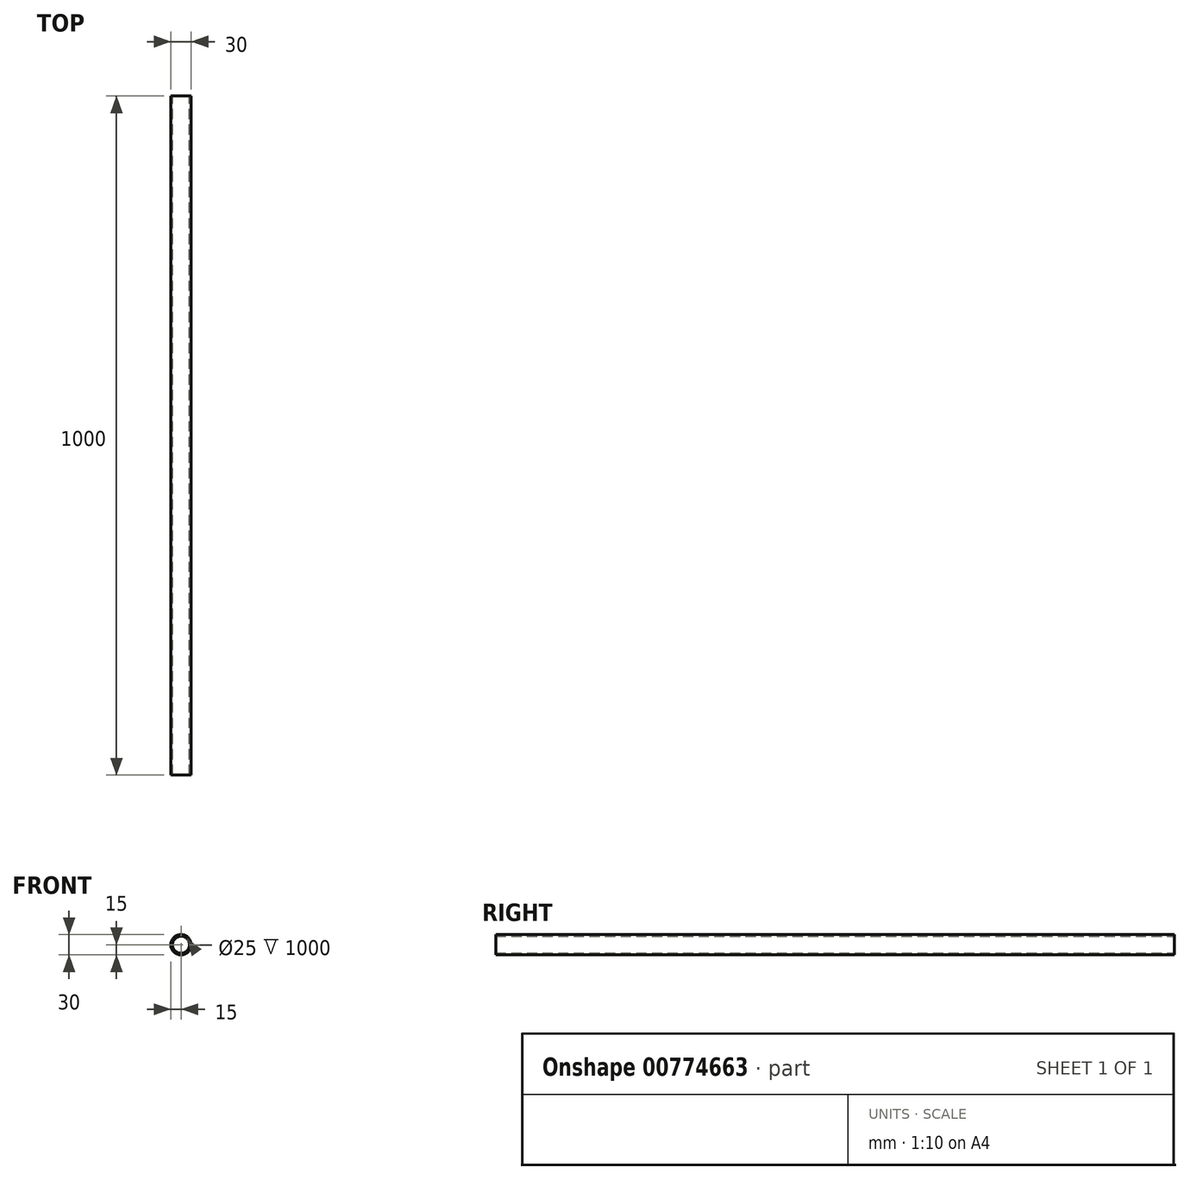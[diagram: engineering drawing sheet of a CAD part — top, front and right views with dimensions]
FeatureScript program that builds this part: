
annotation { "Feature Type Name" : "Feature", "Feature Type Description" : "" }
export const myFeature = defineFeature(function(context is Context, id is Id, definition is map)
    precondition{}
    {
        {
            var Q0;
            Q0=qCreatedBy(makeId("Front.planeOp"),FACE);
            var sketch = newSketch(context, id + "F0", { "sketchPlane" : qUnion([Q0])});
            skCircle(sketch, "E0", {"center": v(0, 0) * mm, "radius": 12.5 * mm});
            skCircle(sketch, "E1", {"center": v(0, 0) * mm, "radius": 15 * mm});
            skSolve(sketch);
        }
        {
            var Q0;
            Q0=makeQuery(id+"F0.imprint","IMPRINT",FACE,{"disambiguationData":[TD([[makeQuery(id+"F0.imprint","IMPRINT",EDGE,{"derivedFrom":sQuery(id+"F0.wireOp",EDGE,"E0")}),-1.0]])]});
            extrude(context, id + "F1", {"entities" : qUnion([Q0]), "depth" : 1000 * mm, "offsetDistance" : 25 * mm});
        }
    });
